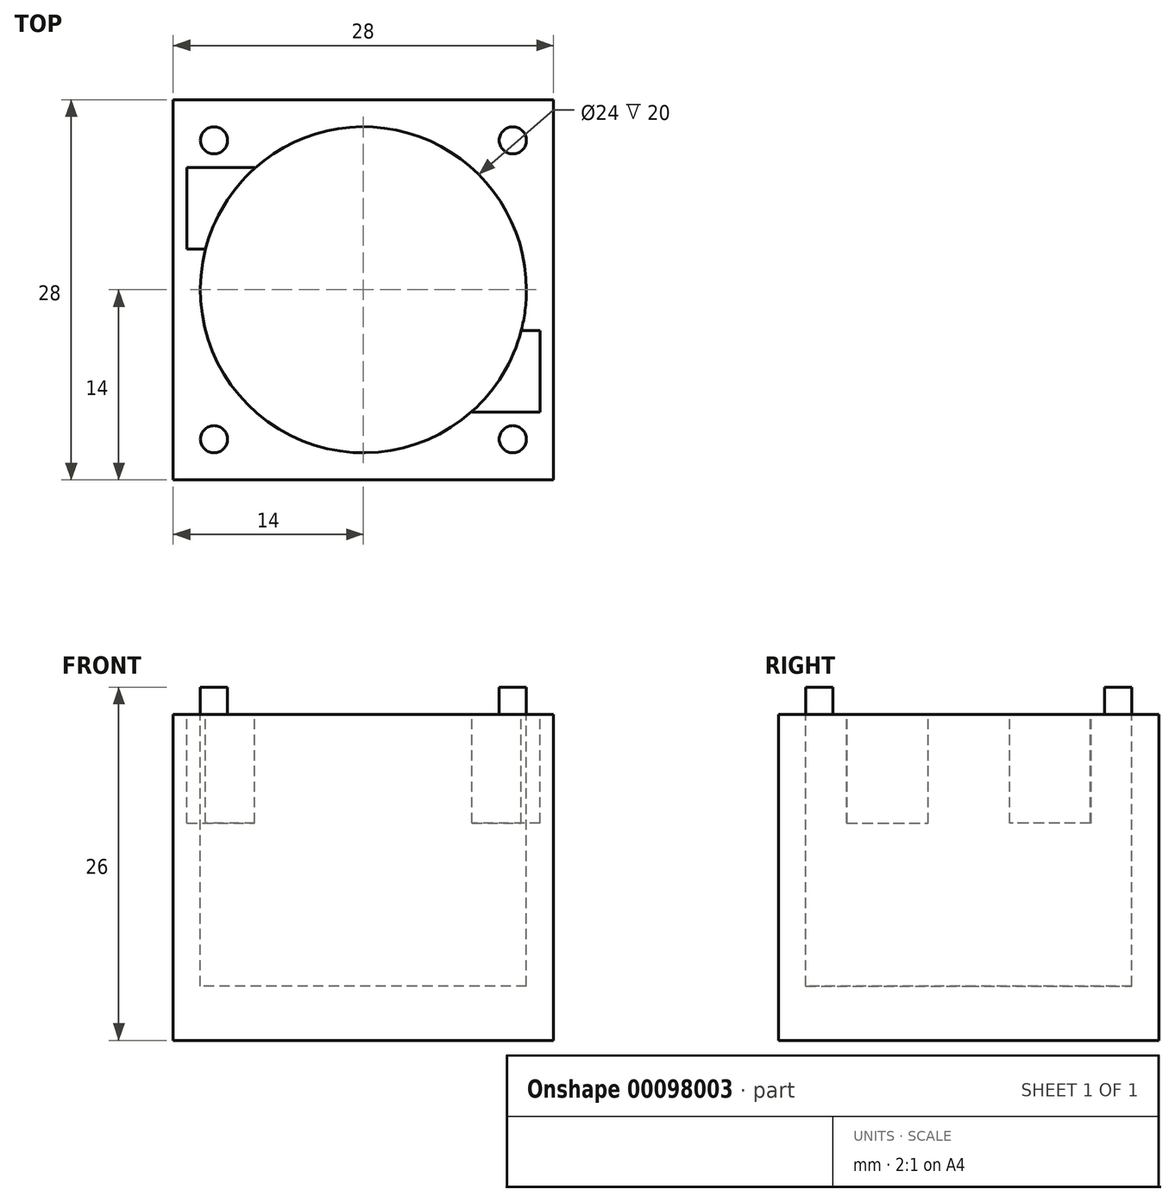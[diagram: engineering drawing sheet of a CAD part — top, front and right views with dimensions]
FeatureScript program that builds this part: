
annotation { "Feature Type Name" : "Feature", "Feature Type Description" : "" }
export const myFeature = defineFeature(function(context is Context, id is Id, definition is map)
    precondition{}
    {
        {
            var Q0;
            Q0=qCreatedBy(makeId("Top.planeOp"),FACE);
            var sketch = newSketch(context, id + "F0", { "sketchPlane" : qUnion([Q0])});
            skLineSegment(sketch, "E0.bottom", {"start": v(14, -14) * mm, "end": v(-14, -14) * mm});
            skLineSegment(sketch, "E0.top", {"start": v(14, 14) * mm, "end": v(-14, 14) * mm});
            skLineSegment(sketch, "E0.left", {"start": v(14, -14) * mm, "end": v(14, 14) * mm});
            skLineSegment(sketch, "E0.right", {"start": v(-14, -14) * mm, "end": v(-14, 14) * mm});
            skPoint(sketch, "E0.middle", {"position": v(0, 0) * mm});
            skSolve(sketch);
        }
        {
            var Q0;
            Q0=makeQuery(id+"F0.imprint","IMPRINT",FACE,{"disambiguationData":[TD([[makeQuery(id+"F0.imprint","IMPRINT",EDGE,{"derivedFrom":sQuery(id+"F0.wireOp",EDGE,"E0.bottom")}),-1.0]])]});
            extrude(context, id + "F1", {"entities" : qUnion([Q0]), "depth" : 24 * mm});
        }
        {
            var Q0;
            Q0=makeQuery(id+"F1.opExtrude","CAP_FACE",FACE,{"disambiguationData":[OSD([sQuery(id+"F0.wireOp",EDGE,"E0.bottom"),sQuery(id+"F0.wireOp",EDGE,"E0.top"),sQuery(id+"F0.wireOp",EDGE,"E0.left"),sQuery(id+"F0.wireOp",EDGE,"E0.right")])],"isStart":false});
            var sketch = newSketch(context, id + "F2", { "sketchPlane" : qUnion([Q0])});
            skCircle(sketch, "E1", {"center": v(0, 0) * mm, "radius": 12 * mm});
            skSolve(sketch);
        }
        {
            var Q0;
            Q0 = qSketchRegion(id + "F2", true);
            extrude(context, id + "F3", {"entities" : qUnion([Q0]), "operationType" : NewBodyOperationType.REMOVE, "oppositeDirection" : true, "depth" : 20 * mm});
        }
        {
            var Q0;
            Q0=makeQuery(id+"F2.imprint","IMPRINT",FACE,{"disambiguationData":[TD([[makeQuery(id+"F2.imprint","IMPRINT",EDGE,{"derivedFrom":sQuery(id+"F2.wireOp",EDGE,"E1")}),-1.0]])]});
            var sketch = newSketch(context, id + "F4", { "sketchPlane" : qUnion([Q0])});
            skCircle(sketch, "E2", {"center": v(-11, 11) * mm, "radius": 1 * mm});
            skCircle(sketch, "E3", {"center": v(11, 11) * mm, "radius": 1 * mm});
            skCircle(sketch, "E4", {"center": v(11, -11) * mm, "radius": 1 * mm});
            skCircle(sketch, "E5", {"center": v(-11, -11) * mm, "radius": 1 * mm});
            skLineSegment(sketch, "E6", {"start": v(-11, 11) * mm, "end": v(-11, -11) * mm, "construction": true});
            skLineSegment(sketch, "E7", {"start": v(-11, -11) * mm, "end": v(11, -11) * mm, "construction": true});
            skLineSegment(sketch, "E8", {"start": v(11, -11) * mm, "end": v(11, 11) * mm, "construction": true});
            skLineSegment(sketch, "E9", {"start": v(-11, 11) * mm, "end": v(11, 11) * mm, "construction": true});
            skLineSegment(sketch, "E10", {"start": v(0, 0) * mm, "end": v(-11, 11) * mm, "construction": true});
            skLineSegment(sketch, "E11", {"start": v(0, 0) * mm, "end": v(11, 11) * mm, "construction": true});
            skLineSegment(sketch, "E12", {"start": v(0, 0) * mm, "end": v(-11, -11) * mm, "construction": true});
            skLineSegment(sketch, "E13", {"start": v(0, 0) * mm, "end": v(11, -11) * mm, "construction": true});
            skSolve(sketch);
        }
        {
            var Q0;
            Q0 = qSketchRegion(id + "F4", true);
            extrude(context, id + "F5", {"entities" : qUnion([Q0]), "operationType" : NewBodyOperationType.ADD, "depth" : 2 * mm});
        }
        {
            var Q0;
            Q0=makeQuery(id+"F2.imprint","IMPRINT",FACE,{"disambiguationData":[TD([[makeQuery(id+"F2.imprint","IMPRINT",EDGE,{"derivedFrom":sQuery(id+"F2.wireOp",EDGE,"E1")}),-1.0]])]});
            var sketch = newSketch(context, id + "F6", { "sketchPlane" : qUnion([Q0])});
            skLineSegment(sketch, "E14.bottom", {"start": v(-13, 9) * mm, "end": v(-8, 9) * mm});
            skLineSegment(sketch, "E14.top", {"start": v(-13, 3) * mm, "end": v(-8, 3) * mm});
            skLineSegment(sketch, "E14.left", {"start": v(-13, 9) * mm, "end": v(-13, 3) * mm});
            skLineSegment(sketch, "E14.right", {"start": v(-8, 9) * mm, "end": v(-8, 3) * mm});
            skPoint(sketch, "E15.middle", {"position": v(0, 0) * mm});
            skLineSegment(sketch, "E16.bottom", {"start": v(13, -9) * mm, "end": v(8, -9) * mm});
            skLineSegment(sketch, "E16.top", {"start": v(13, -3) * mm, "end": v(8, -3) * mm});
            skLineSegment(sketch, "E16.left", {"start": v(13, -9) * mm, "end": v(13, -3) * mm});
            skLineSegment(sketch, "E16.right", {"start": v(8, -9) * mm, "end": v(8, -3) * mm});
            skSolve(sketch);
        }
        {
            var Q0;
            Q0 = qSketchRegion(id + "F6", true);
            extrude(context, id + "F7", {"entities" : qUnion([Q0]), "operationType" : NewBodyOperationType.REMOVE, "oppositeDirection" : true, "depth" : 8 * mm});
        }
    });
